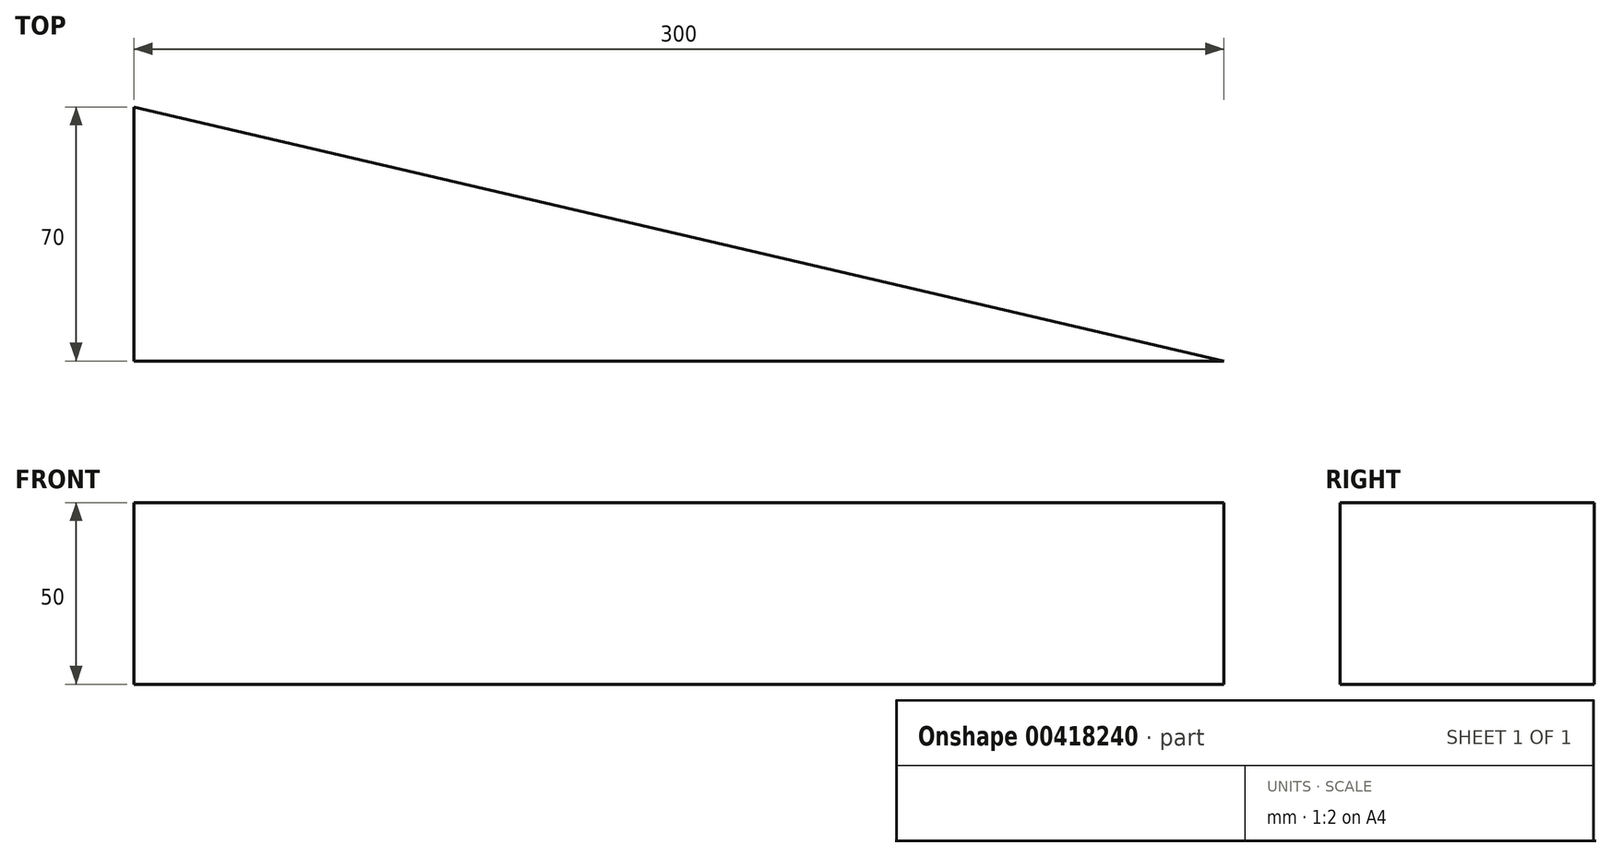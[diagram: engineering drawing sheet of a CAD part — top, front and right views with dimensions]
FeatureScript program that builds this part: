
annotation { "Feature Type Name" : "Feature", "Feature Type Description" : "" }
export const myFeature = defineFeature(function(context is Context, id is Id, definition is map)
    precondition{}
    {
        {
            var Q0;
            Q0=qCreatedBy(makeId("Top.planeOp"),FACE);
            var sketch = newSketch(context, id + "F0", { "sketchPlane" : qUnion([Q0])});
            skLineSegment(sketch, "E0", {"start": v(-67.56, 36.26) * mm, "end": v(-67.56, -33.74) * mm});
            skLineSegment(sketch, "E1", {"start": v(232.44, -33.74) * mm, "end": v(-67.56, 36.26) * mm});
            skLineSegment(sketch, "E2", {"start": v(-67.56, -33.74) * mm, "end": v(232.44, -33.74) * mm});
            skSolve(sketch);
        }
        {
            var Q0;
            Q0=makeQuery(id+"F0.imprint","IMPRINT",FACE,{"disambiguationData":[TD([[makeQuery(id+"F0.imprint","IMPRINT",EDGE,{"derivedFrom":sQuery(id+"F0.wireOp",EDGE,"E0")}),1.0]])]});
            extrude(context, id + "F1", {"entities" : qUnion([Q0]), "depth" : 50 * mm});
        }
    });
